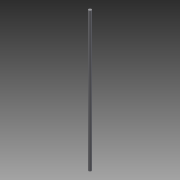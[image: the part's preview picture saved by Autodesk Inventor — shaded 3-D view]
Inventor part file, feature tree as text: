
AUTODESK INVENTOR PART (.ipt)
format: ipt  version: 2015 (Build 190159000, 159)  size: 61,952 bytes
history: native  units: mm
features: extrude x1, sketch x1
ambient origin geometry x8: Origin, YZ Plane, XZ Plane, XY Plane, X Axis, Y Axis, Z Axis, Center Point
bodies: Solid1 (feature_tree)
feature tree (2):
  extrude  "Extrusion1"  Depth=300.0mm TaperAngle=0.0deg
  sketch  "Sketch1"  dims[d0=6.0mm d1=300.0mm d2=0.0mm]
